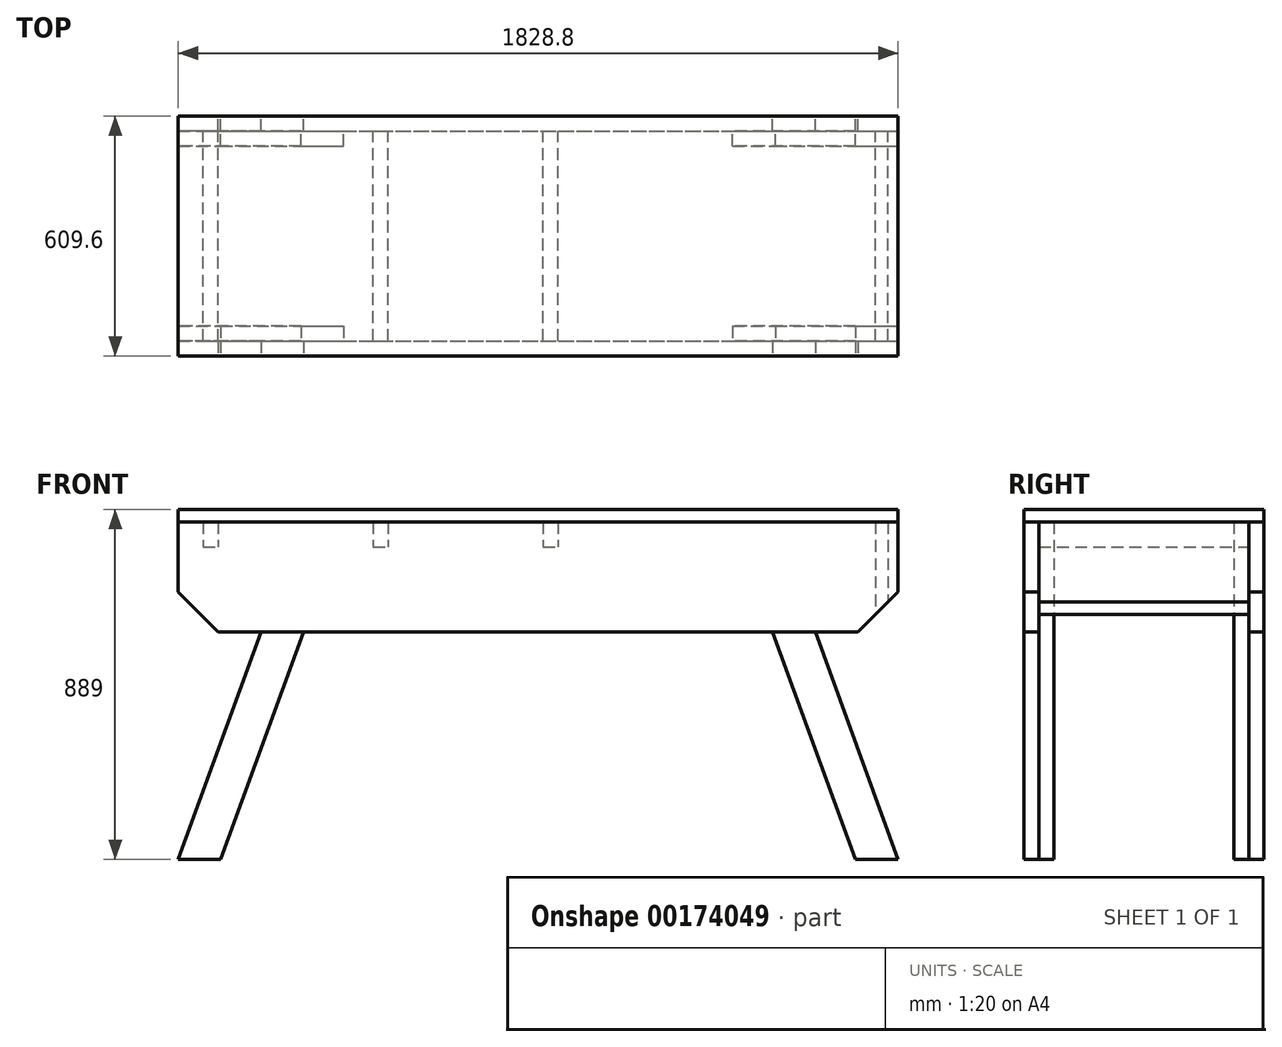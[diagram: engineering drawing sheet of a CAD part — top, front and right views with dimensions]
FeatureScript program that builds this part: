
annotation { "Feature Type Name" : "Feature", "Feature Type Description" : "" }
export const myFeature = defineFeature(function(context is Context, id is Id, definition is map)
    precondition{}
    {
        {
            var Q0;
            Q0=qCreatedBy(makeId("Front.planeOp"),FACE);
            var sketch = newSketch(context, id + "F0", { "sketchPlane" : qUnion([Q0])});
            skLineSegment(sketch, "E0.bottom", {"start": v(-914.4, 889) * mm, "end": v(914.4, 889) * mm});
            skLineSegment(sketch, "E0.top", {"start": v(-914.4, 857.25) * mm, "end": v(914.4, 857.25) * mm});
            skLineSegment(sketch, "E0.left", {"start": v(-914.4, 889) * mm, "end": v(-914.4, 857.25) * mm});
            skLineSegment(sketch, "E0.right", {"start": v(914.4, 889) * mm, "end": v(914.4, 857.25) * mm});
            skLineSegment(sketch, "E1.top", {"start": v(-812.8, 577.85) * mm, "end": v(812.8, 577.85) * mm});
            skLineSegment(sketch, "E1.left", {"start": v(-914.4, 857.25) * mm, "end": v(-914.4, 679.45) * mm});
            skLineSegment(sketch, "E1.right", {"start": v(914.4, 857.25) * mm, "end": v(914.4, 679.45) * mm});
            skLineSegment(sketch, "E2", {"start": v(-602.39, 857.25) * mm, "end": v(-914.4, 0) * mm});
            skLineSegment(sketch, "E3", {"start": v(-914.4, 0) * mm, "end": v(-806.28, 0) * mm});
            skLineSegment(sketch, "E4", {"start": v(-806.28, 0) * mm, "end": v(-494.27, 857.25) * mm});
            skLineSegment(sketch, "E5.MirrorCS", {"start": v(914.4, 0) * mm, "end": v(806.28, 0) * mm});
            skLineSegment(sketch, "E6.MirrorCS", {"start": v(806.28, 0) * mm, "end": v(494.27, 857.25) * mm});
            skLineSegment(sketch, "E7.MirrorCS", {"start": v(602.39, 857.25) * mm, "end": v(914.4, 0) * mm});
            skLineSegment(sketch, "E8", {"start": v(-812.8, 577.85) * mm, "end": v(-914.4, 679.45) * mm});
            skPoint(sketch, "E9", {"position": v(0, 577.85) * mm});
            skLineSegment(sketch, "E10", {"start": v(-602.39, 857.25) * mm, "end": v(-494.27, 857.25) * mm});
            skPoint(sketch, "E11.orphan", {"position": v(-914.4, 577.85) * mm});
            skLineSegment(sketch, "E12.MirrorCS", {"start": v(812.8, 577.85) * mm, "end": v(914.4, 679.45) * mm});
            skPoint(sketch, "E13.orphan", {"position": v(914.4, 577.85) * mm});
            skSolve(sketch);
        }
        {
            var Q0;
            Q0=makeQuery(id+"F0.imprint","IMPRINT",FACE,{"disambiguationData":[TD([[makeQuery(id+"F0.imprint","IMPRINT",EDGE,{"derivedFrom":sQuery(id+"F0.wireOp",EDGE,"E0.bottom")}),-1.0]])]});
            extrude(context, id + "F1", {"entities" : qUnion([Q0]), "depth" : 609.6 * mm});
        }
        {
            var Q0;
            Q0=makeQuery(id+"F0.imprint","IMPRINT",FACE,{"disambiguationData":[TD([[makeQuery(id+"F0.imprint","IMPRINT",EDGE,{"derivedFrom":sQuery(id+"F0.wireOp",EDGE,"E0.top")}),-1.0]])]});
            var Q1;
            {var subQ5=sQuery(id+"F0.wireOp",EDGE,"E10");Q1=makeQuery(id+"F0.imprint","IMPRINT",FACE,{"disambiguationData":[TD([[makeQuery(id+"F0.imprint","IMPRINT",EDGE,{"derivedFrom":subQ5}),-1.0]])]});}
            var Q2;
            {var subQ6=sQuery(id+"F0.wireOp",EDGE,"E1.left");Q2=makeQuery(id+"F0.imprint","IMPRINT",FACE,{"disambiguationData":[TD([[makeQuery(id+"F0.imprint","IMPRINT",EDGE,{"derivedFrom":subQ6}),1.0]])]});}
            var Q3;
            {var subQ0=sQuery(id+"F0.wireOp",EDGE,"E1.right");Q3=makeQuery(id+"F0.imprint","IMPRINT",FACE,{"disambiguationData":[TD([[makeQuery(id+"F0.imprint","IMPRINT",EDGE,{"derivedFrom":subQ0}),-1.0]])]});}
            extrude(context, id + "F2", {"entities" : qUnion([Q0, Q1, Q2, Q3]), "depth" : 38.1 * mm});
        }
        {
            var Q0;
            {var subQ5=sQuery(id+"F0.wireOp",EDGE,"E3");Q0=makeQuery(id+"F0.imprint","IMPRINT",FACE,{"disambiguationData":[TD([[makeQuery(id+"F0.imprint","IMPRINT",EDGE,{"derivedFrom":subQ5}),1.0]])]});}
            var Q1;
            {var subQ5=sQuery(id+"F0.wireOp",EDGE,"E5.MirrorCS");Q1=makeQuery(id+"F0.imprint","IMPRINT",FACE,{"disambiguationData":[TD([[makeQuery(id+"F0.imprint","IMPRINT",EDGE,{"derivedFrom":subQ5}),-1.0]])]});}
            var Q2;
            Q2=makeQuery(id+"F2.opExtrude","CAP_FACE",FACE,{"disambiguationData":[OSD([sQuery(id+"F0.wireOp",EDGE,"E0.top"),sQuery(id+"F0.wireOp",EDGE,"E1.top"),sQuery(id+"F0.wireOp",EDGE,"E1.left"),sQuery(id+"F0.wireOp",EDGE,"E1.right"),sQuery(id+"F0.wireOp",EDGE,"E8"),sQuery(id+"F0.wireOp",EDGE,"E10"),sQuery(id+"F0.wireOp",EDGE,"E12.MirrorCS")])],"isStart":false});
            extrude(context, id + "F3", {"entities" : qUnion([Q0, Q1]), "endBound" : BoundingType.UP_TO_SURFACE, "endBoundEntityFace" : qUnion([Q2]), "depth" : 76.2 * mm});
        }
        {
            var Q0;
            Q0=makeQuery(id+"F2.opExtrude","CAP_FACE",FACE,{"disambiguationData":[OSD([sQuery(id+"F0.wireOp",EDGE,"E0.top"),sQuery(id+"F0.wireOp",EDGE,"E1.top"),sQuery(id+"F0.wireOp",EDGE,"E1.left"),sQuery(id+"F0.wireOp",EDGE,"E1.right"),sQuery(id+"F0.wireOp",EDGE,"E8"),sQuery(id+"F0.wireOp",EDGE,"E10"),sQuery(id+"F0.wireOp",EDGE,"E12.MirrorCS")])],"isStart":false});
            var sketch = newSketch(context, id + "F4", { "sketchPlane" : qUnion([Q0])});
            skLineSegment(sketch, "E14.0", {"start": v(-806.28, 0) * mm, "end": v(-494.27, 857.25) * mm});
            skLineSegment(sketch, "E15.0", {"start": v(-602.39, 857.25) * mm, "end": v(-914.4, 0) * mm});
            skLineSegment(sketch, "E16.0.0", {"start": v(-595.96, 577.85) * mm, "end": v(-704.08, 577.85) * mm});
            skLineSegment(sketch, "E16.0.1", {"start": v(-704.08, 577.85) * mm, "end": v(-914.4, 0) * mm});
            skLineSegment(sketch, "E16.0.2", {"start": v(-914.4, 0) * mm, "end": v(-806.28, 0) * mm});
            skLineSegment(sketch, "E16.0.3", {"start": v(-806.28, 0) * mm, "end": v(-595.96, 577.85) * mm});
            skLineSegment(sketch, "E17.0.0", {"start": v(704.08, 577.85) * mm, "end": v(595.96, 577.85) * mm});
            skLineSegment(sketch, "E17.0.1", {"start": v(595.96, 577.85) * mm, "end": v(806.28, 0) * mm});
            skLineSegment(sketch, "E17.0.2", {"start": v(806.28, 0) * mm, "end": v(914.4, 0) * mm});
            skLineSegment(sketch, "E17.0.3", {"start": v(914.4, 0) * mm, "end": v(704.08, 577.85) * mm});
            skLineSegment(sketch, "E18.0", {"start": v(806.28, 0) * mm, "end": v(494.27, 857.25) * mm});
            skLineSegment(sketch, "E19.0", {"start": v(602.39, 857.25) * mm, "end": v(914.4, 0) * mm});
            skLineSegment(sketch, "E20.0", {"start": v(-914.4, 857.25) * mm, "end": v(914.4, 857.25) * mm});
            skSolve(sketch);
        }
        {
            var Q0;
            {var subQ0=sQuery(id+"F4.wireOp",EDGE,"E14.0");Q0=makeQuery(id+"F4.imprint","IMPRINT",FACE,{"disambiguationData":[TD([[makeQuery(id+"F4.imprint","IMPRINT",EDGE,{"derivedFrom":subQ0}),1.0]])]});}
            var Q1;
            Q1=makeQuery(id+"F4.imprint","IMPRINT",FACE,{"disambiguationData":[TD([[makeQuery(id+"F4.imprint","IMPRINT",EDGE,{"derivedFrom":sQuery(id+"F4.wireOp",EDGE,"E16.0.0")}),-1.0]])]});
            var Q2;
            {var subQ0=sQuery(id+"F4.wireOp",EDGE,"E17.0.0");Q2=makeQuery(id+"F4.imprint","IMPRINT",FACE,{"disambiguationData":[TD([[makeQuery(id+"F4.imprint","IMPRINT",EDGE,{"derivedFrom":subQ0}),1.0]])]});}
            var Q3;
            {var subQ0=sQuery(id+"F4.wireOp",EDGE,"E17.0.0");Q3=makeQuery(id+"F4.imprint","IMPRINT",FACE,{"disambiguationData":[TD([[makeQuery(id+"F4.imprint","IMPRINT",EDGE,{"derivedFrom":subQ0}),-1.0]])]});}
            extrude(context, id + "F5", {"entities" : qUnion([Q0, Q1, Q2, Q3]), "depth" : 38.1 * mm});
        }
        {
            var Q0;
            Q0=makeQuery(id+"F2.opExtrude","CAP_FACE",FACE,{"disambiguationData":[OSD([sQuery(id+"F0.wireOp",EDGE,"E0.top"),sQuery(id+"F0.wireOp",EDGE,"E1.top"),sQuery(id+"F0.wireOp",EDGE,"E1.left"),sQuery(id+"F0.wireOp",EDGE,"E1.right"),sQuery(id+"F0.wireOp",EDGE,"E8"),sQuery(id+"F0.wireOp",EDGE,"E10"),sQuery(id+"F0.wireOp",EDGE,"E12.MirrorCS")])],"isStart":false});
            var sketch = newSketch(context, id + "F6", { "sketchPlane" : qUnion([Q0])});
            skLineSegment(sketch, "E21.bottom", {"start": v(-419.1, 857.25) * mm, "end": v(-381, 857.25) * mm});
            skLineSegment(sketch, "E21.top", {"start": v(-419.1, 793.75) * mm, "end": v(-381, 793.75) * mm});
            skLineSegment(sketch, "E21.left", {"start": v(-419.1, 857.25) * mm, "end": v(-419.1, 793.75) * mm});
            skLineSegment(sketch, "E21.right", {"start": v(-381, 857.25) * mm, "end": v(-381, 793.75) * mm});
            skPoint(sketch, "E22.oppositeSnap0", {"position": v(0, 857.25) * mm});
            skLineSegment(sketch, "E22.bottom", {"start": v(12.7, 857.25) * mm, "end": v(50.8, 857.25) * mm});
            skLineSegment(sketch, "E22.top", {"start": v(12.7, 793.75) * mm, "end": v(50.8, 793.75) * mm});
            skLineSegment(sketch, "E22.left", {"start": v(12.7, 857.25) * mm, "end": v(12.7, 793.75) * mm});
            skLineSegment(sketch, "E22.right", {"start": v(50.8, 857.25) * mm, "end": v(50.8, 793.75) * mm});
            skLineSegment(sketch, "E23.bottom", {"start": v(444.5, 857.25) * mm, "end": v(482.6, 857.25) * mm});
            skLineSegment(sketch, "E23.top", {"start": v(444.5, 793.75) * mm, "end": v(482.6, 793.75) * mm});
            skLineSegment(sketch, "E23.left", {"start": v(444.5, 857.25) * mm, "end": v(444.5, 793.75) * mm});
            skLineSegment(sketch, "E23.right", {"start": v(482.6, 857.25) * mm, "end": v(482.6, 793.75) * mm});
            skLineSegment(sketch, "E24.bottom", {"start": v(-850.9, 857.25) * mm, "end": v(-812.8, 857.25) * mm});
            skLineSegment(sketch, "E24.top", {"start": v(-850.9, 793.75) * mm, "end": v(-812.8, 793.75) * mm});
            skLineSegment(sketch, "E24.left", {"start": v(-850.9, 857.25) * mm, "end": v(-850.9, 793.75) * mm});
            skLineSegment(sketch, "E24.right", {"start": v(-812.8, 857.25) * mm, "end": v(-812.8, 793.75) * mm});
            skLineSegment(sketch, "E25.bottom", {"start": v(857.25, 857.25) * mm, "end": v(889, 857.25) * mm});
            skLineSegment(sketch, "E25.left", {"start": v(857.25, 857.25) * mm, "end": v(857.25, 622.3) * mm});
            skLineSegment(sketch, "E25.right", {"start": v(889, 857.25) * mm, "end": v(889, 654.05) * mm});
            skLineSegment(sketch, "E26.0", {"start": v(812.8, 577.85) * mm, "end": v(914.4, 679.45) * mm});
            skSolve(sketch);
        }
        {
            var Q0;
            Q0=makeQuery(id+"F1.opExtrude","CAP_FACE",FACE,{"disambiguationData":[OSD([sQuery(id+"F0.wireOp",EDGE,"E0.bottom"),sQuery(id+"F0.wireOp",EDGE,"E0.left"),sQuery(id+"F0.wireOp",EDGE,"E0.right"),sQuery(id+"F0.wireOp",EDGE,"E0.top"),sQuery(id+"F0.wireOp",EDGE,"E10")])],"isStart":false});
            var sketch = newSketch(context, id + "F7", { "sketchPlane" : qUnion([Q0])});
            skLineSegment(sketch, "E27.0.0", {"start": v(494.27, 857.25) * mm, "end": v(-494.27, 857.25) * mm});
            skLineSegment(sketch, "E27.0.1", {"start": v(-494.27, 857.25) * mm, "end": v(-595.96, 577.85) * mm});
            skLineSegment(sketch, "E27.0.2", {"start": v(-595.96, 577.85) * mm, "end": v(595.96, 577.85) * mm});
            skLineSegment(sketch, "E27.0.3", {"start": v(595.96, 577.85) * mm, "end": v(494.27, 857.25) * mm});
            skLineSegment(sketch, "E28.0.0", {"start": v(602.39, 857.25) * mm, "end": v(494.27, 857.25) * mm});
            skLineSegment(sketch, "E28.0.1", {"start": v(494.27, 857.25) * mm, "end": v(595.96, 577.85) * mm});
            skLineSegment(sketch, "E28.0.2", {"start": v(595.96, 577.85) * mm, "end": v(704.08, 577.85) * mm});
            skLineSegment(sketch, "E28.0.3", {"start": v(704.08, 577.85) * mm, "end": v(602.39, 857.25) * mm});
            skLineSegment(sketch, "E28.1.0", {"start": v(914.4, 857.25) * mm, "end": v(602.39, 857.25) * mm});
            skLineSegment(sketch, "E28.1.1", {"start": v(602.39, 857.25) * mm, "end": v(704.08, 577.85) * mm});
            skLineSegment(sketch, "E28.1.2", {"start": v(704.08, 577.85) * mm, "end": v(812.8, 577.85) * mm});
            skLineSegment(sketch, "E28.1.3", {"start": v(812.8, 577.85) * mm, "end": v(914.4, 679.45) * mm});
            skLineSegment(sketch, "E28.1.4", {"start": v(914.4, 679.45) * mm, "end": v(914.4, 857.25) * mm});
            skLineSegment(sketch, "E28.2.0", {"start": v(-602.39, 857.25) * mm, "end": v(-704.08, 577.85) * mm});
            skLineSegment(sketch, "E28.2.1", {"start": v(-704.08, 577.85) * mm, "end": v(-595.96, 577.85) * mm});
            skLineSegment(sketch, "E28.2.2", {"start": v(-595.96, 577.85) * mm, "end": v(-494.27, 857.25) * mm});
            skLineSegment(sketch, "E28.2.3", {"start": v(-494.27, 857.25) * mm, "end": v(-602.39, 857.25) * mm});
            skLineSegment(sketch, "E28.3.0", {"start": v(-602.39, 857.25) * mm, "end": v(-914.4, 857.25) * mm});
            skLineSegment(sketch, "E28.3.1", {"start": v(-914.4, 857.25) * mm, "end": v(-914.4, 679.45) * mm});
            skLineSegment(sketch, "E28.3.2", {"start": v(-914.4, 679.45) * mm, "end": v(-812.8, 577.85) * mm});
            skLineSegment(sketch, "E28.3.3", {"start": v(-812.8, 577.85) * mm, "end": v(-704.08, 577.85) * mm});
            skLineSegment(sketch, "E28.3.4", {"start": v(-704.08, 577.85) * mm, "end": v(-602.39, 857.25) * mm});
            skSolve(sketch);
        }
        {
            var Q0;
            Q0=makeQuery(id+"F7.imprint","IMPRINT",FACE,{"disambiguationData":[TD([[makeQuery(id+"F7.imprint","IMPRINT",EDGE,{"derivedFrom":sQuery(id+"F7.wireOp",EDGE,"E28.3.0")}),-1.0]])]});
            var Q1;
            Q1=makeQuery(id+"F7.imprint","IMPRINT",FACE,{"disambiguationData":[TD([[makeQuery(id+"F7.imprint","IMPRINT",EDGE,{"derivedFrom":sQuery(id+"F7.wireOp",EDGE,"E28.2.1")}),1.0]])]});
            var Q2;
            Q2=makeQuery(id+"F7.imprint","IMPRINT",FACE,{"disambiguationData":[TD([[makeQuery(id+"F7.imprint","IMPRINT",EDGE,{"derivedFrom":sQuery(id+"F7.wireOp",EDGE,"E27.0.0")}),-1.0]])]});
            var Q3;
            Q3=makeQuery(id+"F7.imprint","IMPRINT",FACE,{"disambiguationData":[TD([[makeQuery(id+"F7.imprint","IMPRINT",EDGE,{"derivedFrom":sQuery(id+"F7.wireOp",EDGE,"E28.0.0")}),-1.0]])]});
            var Q4;
            Q4=makeQuery(id+"F7.imprint","IMPRINT",FACE,{"disambiguationData":[TD([[makeQuery(id+"F7.imprint","IMPRINT",EDGE,{"derivedFrom":sQuery(id+"F7.wireOp",EDGE,"E28.1.0")}),-1.0]])]});
            extrude(context, id + "F8", {"entities" : qUnion([Q0, Q1, Q2, Q3, Q4]), "oppositeDirection" : true, "depth" : 38.1 * mm});
        }
        {
            var Q0;
            Q0=makeQuery(id+"F1.opExtrude","SWEPT_EDGE",EDGE,{"disambiguationData":[OSD([sQuery(id+"F0.wireOp",EDGE,"E0.right"),sQuery(id+"F0.wireOp",EDGE,"E0.top"),sQuery(id+"F0.wireOp",EDGE,"E1.right")])]});
            cPoint(context, id + "F9", {"entities" : qUnion([Q0]), "parameter" : 0.5});
        }
        {
            var Q0;
            Q0=qCreatedBy(makeId("Front.planeOp"),FACE);
            var Q1;
            Q1 = qCreatedBy(id + "F9" ,VERTEX);
            cPlane(context, id + "F10", {"entities" : qUnion([Q0, Q1]), "cplaneType" : CPlaneType.PLANE_POINT, "offset" : 25.4 * mm, "width" : 152.4 * mm, "height" : 152.4 * mm});
        }
        {
            var Q0;
            Q0=makeQuery(id+"F5.opExtrude","SWEPT_BODY",BODY,{"disambiguationData":[OSD([sQuery(id+"F4.wireOp",EDGE,"E17.0.2"),sQuery(id+"F4.wireOp",EDGE,"E18.0"),sQuery(id+"F4.wireOp",EDGE,"E19.0"),sQuery(id+"F4.wireOp",EDGE,"E20.0")])]});
            var Q1;
            Q1=makeQuery(id+"F5.opExtrude","SWEPT_BODY",BODY,{"disambiguationData":[OSD([sQuery(id+"F4.wireOp",EDGE,"E14.0"),sQuery(id+"F4.wireOp",EDGE,"E15.0"),sQuery(id+"F4.wireOp",EDGE,"E16.0.1"),sQuery(id+"F4.wireOp",EDGE,"E16.0.2"),sQuery(id+"F4.wireOp",EDGE,"E16.0.3"),sQuery(id+"F4.wireOp",EDGE,"E20.0")])]});
            var Q2;
            Q2=makeQuery(id+"F3.opExtrude","SWEPT_BODY",BODY,{"disambiguationData":[OSD([sQuery(id+"F0.wireOp",EDGE,"E1.top"),sQuery(id+"F0.wireOp",EDGE,"E2"),sQuery(id+"F0.wireOp",EDGE,"E3"),sQuery(id+"F0.wireOp",EDGE,"E4")])]});
            var Q3;
            Q3=makeQuery(id+"F3.opExtrude","SWEPT_BODY",BODY,{"disambiguationData":[OSD([sQuery(id+"F0.wireOp",EDGE,"E1.top"),sQuery(id+"F0.wireOp",EDGE,"E5.MirrorCS"),sQuery(id+"F0.wireOp",EDGE,"E6.MirrorCS"),sQuery(id+"F0.wireOp",EDGE,"E7.MirrorCS")])]});
            var Q4;
            Q4=qCreatedBy(id+"F10.planeOp",FACE);
            mirror(context, id + "F11", {"entities" : qUnion([Q0, Q1, Q2, Q3]), "mirrorPlane" : qUnion([Q4])});
        }
        {
            var Q0;
            Q0=makeQuery(id+"F6.imprint","IMPRINT",FACE,{"disambiguationData":[TD([[makeQuery(id+"F6.imprint","IMPRINT",EDGE,{"derivedFrom":sQuery(id+"F6.wireOp",EDGE,"E24.bottom")}),-1.0]])]});
            var Q1;
            Q1=makeQuery(id+"F6.imprint","IMPRINT",FACE,{"disambiguationData":[TD([[makeQuery(id+"F6.imprint","IMPRINT",EDGE,{"derivedFrom":sQuery(id+"F6.wireOp",EDGE,"E21.bottom")}),-1.0]])]});
            var Q2;
            Q2=makeQuery(id+"F6.imprint","IMPRINT",FACE,{"disambiguationData":[TD([[makeQuery(id+"F6.imprint","IMPRINT",EDGE,{"derivedFrom":sQuery(id+"F6.wireOp",EDGE,"E22.bottom")}),-1.0]])]});
            var Q3;
            Q3=makeQuery(id+"F6.imprint","IMPRINT",FACE,{"disambiguationData":[TD([[makeQuery(id+"F6.imprint","IMPRINT",EDGE,{"derivedFrom":sQuery(id+"F6.wireOp",EDGE,"E25.bottom")}),-1.0]])]});
            extrude(context, id + "F12", {"entities" : qUnion([Q0, Q1, Q2, Q3]), "endBound" : BoundingType.UP_TO_NEXT, "depth" : 25.4 * mm});
        }
    });
